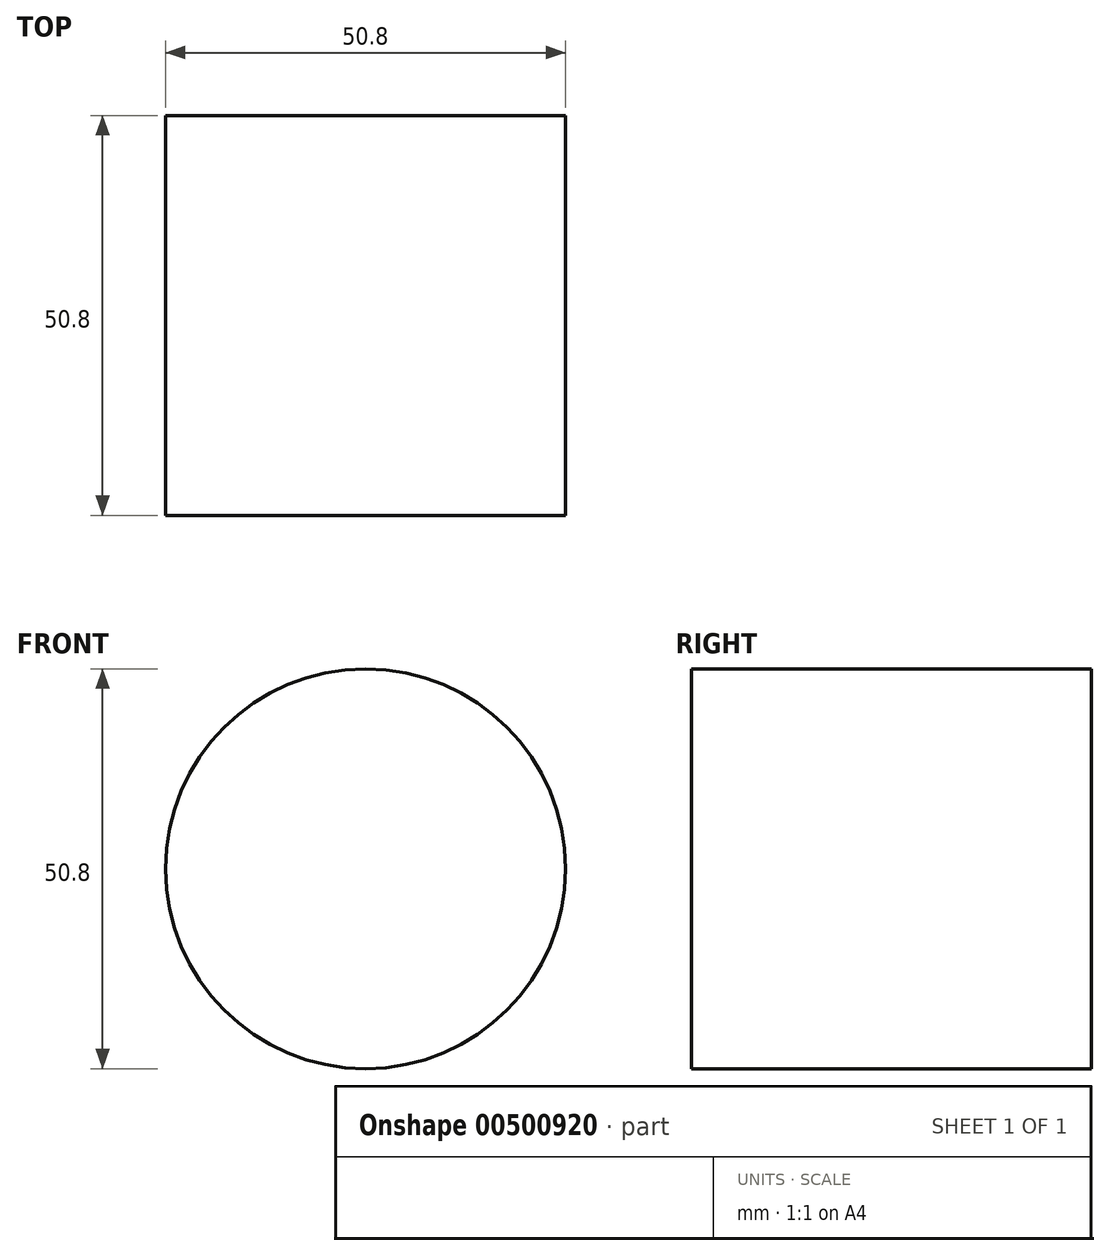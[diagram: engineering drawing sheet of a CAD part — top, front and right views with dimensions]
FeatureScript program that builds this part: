
annotation { "Feature Type Name" : "Feature", "Feature Type Description" : "" }
export const myFeature = defineFeature(function(context is Context, id is Id, definition is map)
    precondition{}
    {
        {
            var Q0;
            Q0=qCreatedBy(makeId("Front.planeOp"),FACE);
            var sketch = newSketch(context, id + "F0", { "sketchPlane" : qUnion([Q0])});
            skCircle(sketch, "E0", {"center": v(0, 0) * mm, "radius": 25.4 * mm});
            skSolve(sketch);
        }
        {
            var Q0;
            Q0=makeQuery(id+"F0.imprint","IMPRINT",FACE,{"disambiguationData":[TD([[makeQuery(id+"F0.imprint","IMPRINT",EDGE,{"derivedFrom":sQuery(id+"F0.wireOp",EDGE,"E0")}),1.0]])]});
            extrude(context, id + "F1", {"entities" : qUnion([Q0]), "oppositeDirection" : true, "depth" : 50.8 * mm, "symmetric" : true});
        }
    });
